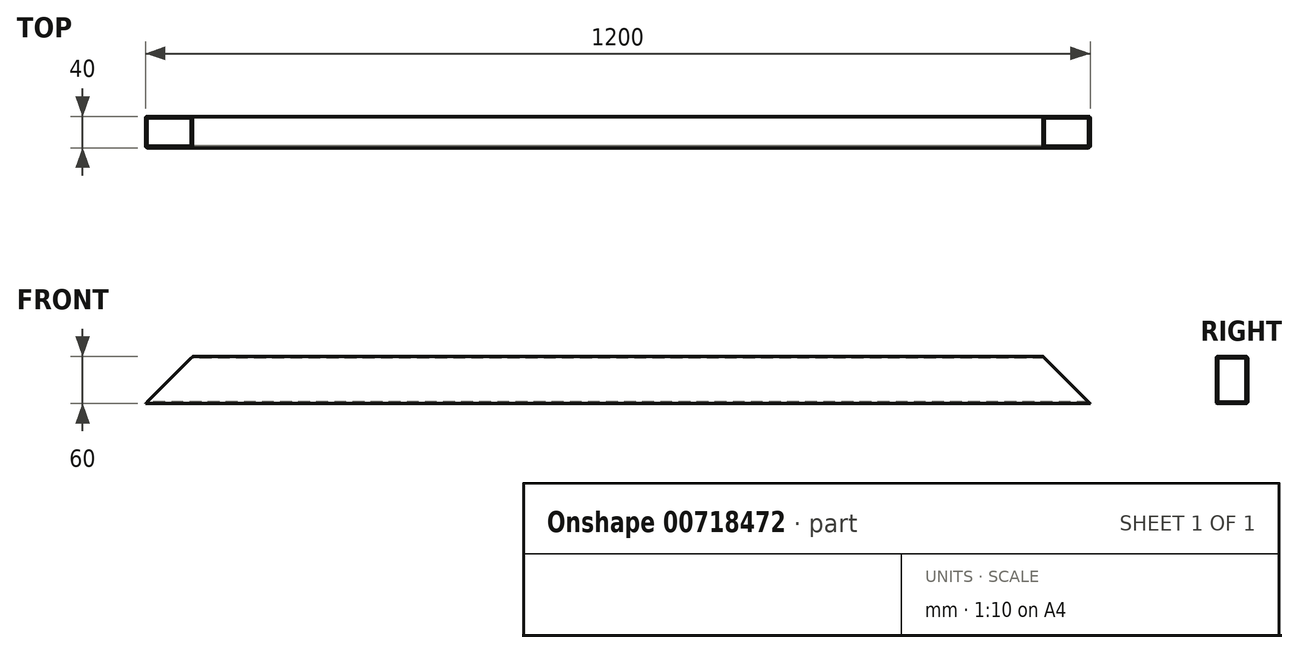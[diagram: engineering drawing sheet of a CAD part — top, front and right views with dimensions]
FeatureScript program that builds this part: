
annotation { "Feature Type Name" : "Feature", "Feature Type Description" : "" }
export const myFeature = defineFeature(function(context is Context, id is Id, definition is map)
    precondition{}
    {
        {
            var Q0;
            Q0=qCreatedBy(makeId("Right.planeOp"),FACE);
            var sketch = newSketch(context, id + "F0", { "sketchPlane" : qUnion([Q0])});
            skLineSegment(sketch, "E0.bottom", {"start": v(-18, -30) * mm, "end": v(18, -30) * mm});
            skLineSegment(sketch, "E0.top", {"start": v(-18, 30) * mm, "end": v(18, 30) * mm});
            skLineSegment(sketch, "E0.left", {"start": v(-20, -28) * mm, "end": v(-20, 28) * mm});
            skLineSegment(sketch, "E0.right", {"start": v(20, -28) * mm, "end": v(20, 28) * mm});
            skPoint(sketch, "E0.middle", {"position": v(0, 0) * mm});
            skLineSegment(sketch, "E1.bottom", {"start": v(-17, -28) * mm, "end": v(17, -28) * mm});
            skLineSegment(sketch, "E1.top", {"start": v(-17, 28) * mm, "end": v(17, 28) * mm});
            skLineSegment(sketch, "E1.left", {"start": v(-18, -27) * mm, "end": v(-18, 27) * mm});
            skLineSegment(sketch, "E1.right", {"start": v(18, -27) * mm, "end": v(18, 27) * mm});
            skPoint(sketch, "E2.visualSharp", {"position": v(-20, 30) * mm});
            skArc(sketch, "E2.filletArc", {"start": v(-18, 30) * mm, "mid": v(-19.41, 29.41) * mm, "end": v(-20, 28) * mm});
            skPoint(sketch, "E3.visualSharp", {"position": v(20, 30) * mm});
            skArc(sketch, "E3.filletArc", {"start": v(20, 28) * mm, "mid": v(19.41, 29.41) * mm, "end": v(18, 30) * mm});
            skPoint(sketch, "E4.visualSharp", {"position": v(20, -30) * mm});
            skArc(sketch, "E4.filletArc", {"start": v(18, -30) * mm, "mid": v(19.41, -29.41) * mm, "end": v(20, -28) * mm});
            skPoint(sketch, "E5.visualSharp", {"position": v(-20, -30) * mm});
            skArc(sketch, "E5.filletArc", {"start": v(-20, -28) * mm, "mid": v(-19.41, -29.41) * mm, "end": v(-18, -30) * mm});
            skArc(sketch, "E6.filletArc", {"start": v(-18, -27) * mm, "mid": v(-17.7, -27.7) * mm, "end": v(-17, -28) * mm});
            skArc(sketch, "E7.filletArc", {"start": v(-17, 28) * mm, "mid": v(-17.7, 27.7) * mm, "end": v(-18, 27) * mm});
            skArc(sketch, "E8.filletArc", {"start": v(18, 27) * mm, "mid": v(17.7, 27.7) * mm, "end": v(17, 28) * mm});
            skArc(sketch, "E9.filletArc", {"start": v(17, -28) * mm, "mid": v(17.7, -27.7) * mm, "end": v(18, -27) * mm});
            skSolve(sketch);
        }
        {
            var Q0;
            Q0=makeQuery(id+"F0.imprint","IMPRINT",FACE,{"disambiguationData":[TD([[makeQuery(id+"F0.imprint","IMPRINT",EDGE,{"derivedFrom":sQuery(id+"F0.wireOp",EDGE,"E0.bottom")}),1.0]])]});
            extrude(context, id + "F1", {"entities" : qUnion([Q0]), "depth" : 600 * mm, "offsetDistance" : 25 * mm, "hasSecondDirection" : true, "secondDirectionOppositeDirection" : true, "secondDirectionDepth" : 600 * mm});
        }
        {
            var Q0;
            Q0=qCreatedBy(makeId("Front.planeOp"),FACE);
            var sketch = newSketch(context, id + "F2", { "sketchPlane" : qUnion([Q0])});
            skLineSegment(sketch, "E10", {"start": v(-600, -30) * mm, "end": v(-600, 30) * mm});
            skLineSegment(sketch, "E11", {"start": v(-600, 30) * mm, "end": v(-540, 30) * mm});
            skLineSegment(sketch, "E12", {"start": v(-540, 30) * mm, "end": v(-600, -30) * mm});
            skLineSegment(sketch, "E13", {"start": v(0, 100.56) * mm, "end": v(0, -96.84) * mm, "construction": true});
            skLineSegment(sketch, "E14.MirrorCS", {"start": v(600, -30) * mm, "end": v(600, 30) * mm});
            skLineSegment(sketch, "E15.MirrorCS", {"start": v(540, 30) * mm, "end": v(600, -30) * mm});
            skLineSegment(sketch, "E16.MirrorCS", {"start": v(600, 30) * mm, "end": v(540, 30) * mm});
            skSolve(sketch);
        }
        {
            var Q0;
            Q0=qSketchRegion(id+"F2",true);
            extrude(context, id + "F3", {"entities" : qUnion([Q0]), "operationType" : NewBodyOperationType.REMOVE, "oppositeDirection" : true, "depth" : 25 * mm, "offsetDistance" : 25 * mm, "hasSecondDirection" : true, "secondDirectionOppositeDirection" : false, "secondDirectionDepth" : 25 * mm});
        }
    });
